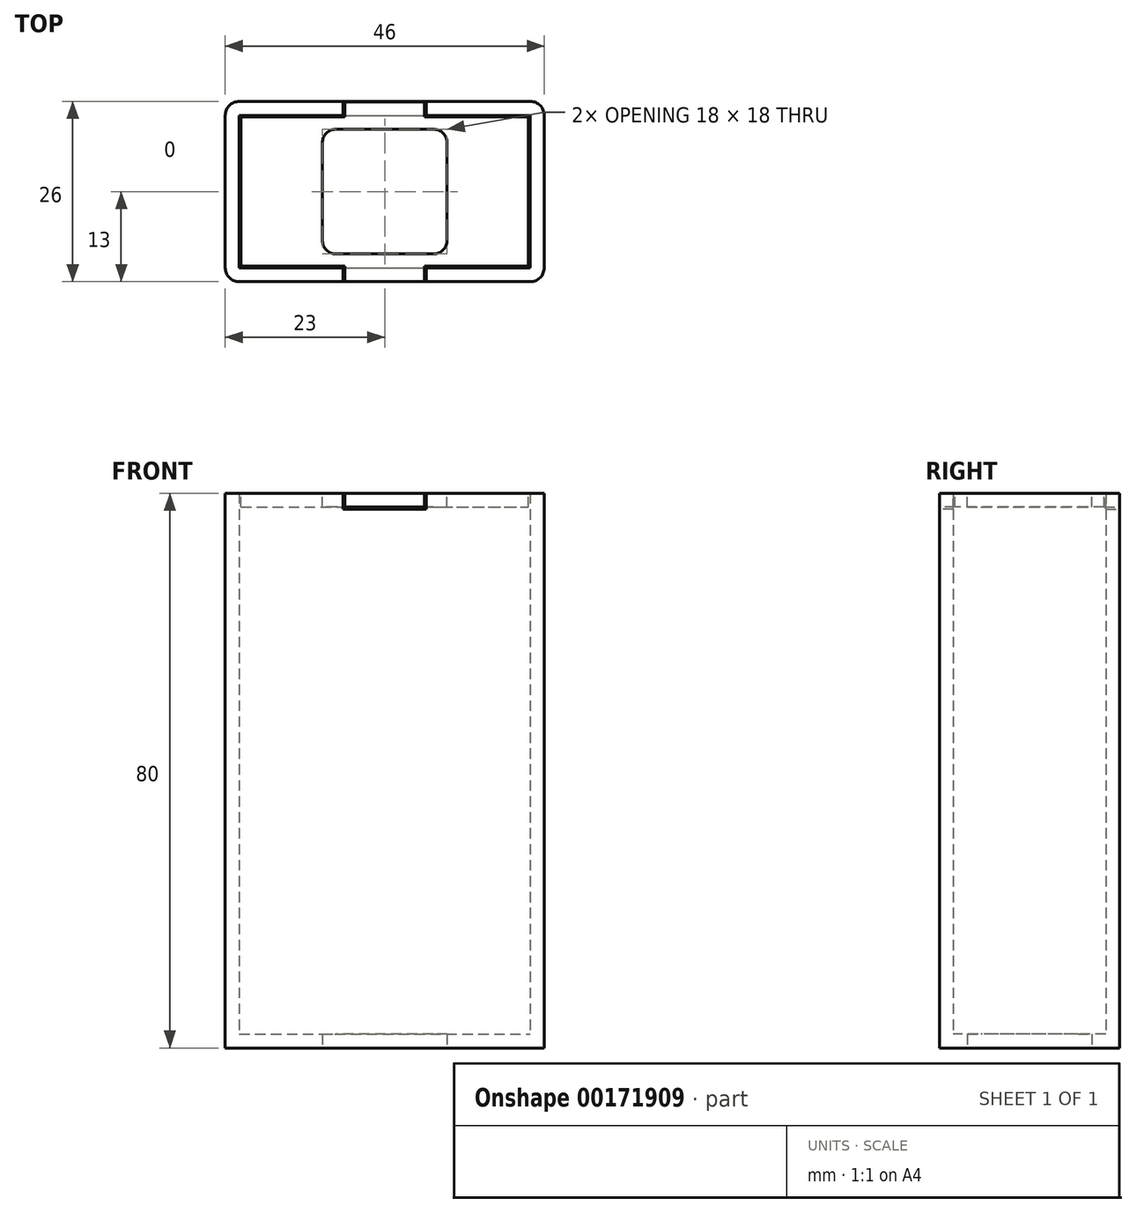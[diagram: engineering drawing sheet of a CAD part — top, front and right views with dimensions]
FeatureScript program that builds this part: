
annotation { "Feature Type Name" : "Feature", "Feature Type Description" : "" }
export const myFeature = defineFeature(function(context is Context, id is Id, definition is map)
    precondition{}
    {
        {
            var Q0;
            Q0=qCreatedBy(makeId("Top.planeOp"),FACE);
            var sketch = newSketch(context, id + "F0", { "sketchPlane" : qUnion([Q0])});
            skLineSegment(sketch, "E0.bottom", {"start": v(-23, 13) * mm, "end": v(23, 13) * mm});
            skLineSegment(sketch, "E0.top", {"start": v(-23, -13) * mm, "end": v(23, -13) * mm});
            skLineSegment(sketch, "E0.left", {"start": v(-23, 13) * mm, "end": v(-23, -13) * mm});
            skLineSegment(sketch, "E0.right", {"start": v(23, 13) * mm, "end": v(23, -13) * mm});
            skPoint(sketch, "E0.middle", {"position": v(0, 0) * mm});
            skSolve(sketch);
        }
        {
            var Q0;
            Q0 = qSketchRegion(id + "F0", true);
            extrude(context, id + "F1", {"entities" : qUnion([Q0]), "depth" : 80 * mm});
        }
        {
            var Q0;
            Q0=makeQuery(id+"F1.opExtrude","CAP_FACE",FACE,{"disambiguationData":[OSD([sQuery(id+"F0.wireOp",EDGE,"E0.bottom"),sQuery(id+"F0.wireOp",EDGE,"E0.top"),sQuery(id+"F0.wireOp",EDGE,"E0.left"),sQuery(id+"F0.wireOp",EDGE,"E0.right")])],"isStart":false});
            shell(context, id + "F2", {"entities" : qUnion([Q0]), "thickness" : 2 * mm});
        }
        {
            var Q0;
            Q0=makeQuery(id+"F1.opExtrude","CAP_FACE",FACE,{"disambiguationData":[OSD([sQuery(id+"F0.wireOp",EDGE,"E0.bottom"),sQuery(id+"F0.wireOp",EDGE,"E0.top"),sQuery(id+"F0.wireOp",EDGE,"E0.left"),sQuery(id+"F0.wireOp",EDGE,"E0.right")])],"isStart":false});
            var sketch = newSketch(context, id + "F3", { "sketchPlane" : qUnion([Q0])});
            skLineSegment(sketch, "E1.bottom", {"start": v(-6, 11) * mm, "end": v(6, 11) * mm});
            skLineSegment(sketch, "E1.top", {"start": v(-6, 13) * mm, "end": v(6, 13) * mm});
            skLineSegment(sketch, "E1.left", {"start": v(-6, 11) * mm, "end": v(-6, 13) * mm});
            skLineSegment(sketch, "E1.right", {"start": v(6, 11) * mm, "end": v(6, 13) * mm});
            skLineSegment(sketch, "E2.MirrorCS", {"start": v(-6, -13) * mm, "end": v(6, -13) * mm});
            skLineSegment(sketch, "E3.MirrorCS", {"start": v(-6, -11) * mm, "end": v(-6, -13) * mm});
            skLineSegment(sketch, "E4.MirrorCS", {"start": v(6, -11) * mm, "end": v(6, -13) * mm});
            skLineSegment(sketch, "E5.MirrorCS", {"start": v(-6, -11) * mm, "end": v(6, -11) * mm});
            skSolve(sketch);
        }
        {
            var Q0;
            Q0 = qSketchRegion(id + "F3", true);
            extrude(context, id + "F4", {"entities" : qUnion([Q0]), "operationType" : NewBodyOperationType.REMOVE, "oppositeDirection" : true, "depth" : 2.3 * mm});
        }
        {
            var Q0;
            Q0=qCreatedBy(makeId("Top.planeOp"),FACE);
            cPlane(context, id + "F5", {"entities" : qUnion([Q0]), "cplaneType" : CPlaneType.OFFSET, "offset" : 80 * mm, "width" : 150 * mm, "height" : 150 * mm});
        }
        {
            var Q0;
            Q0=qCreatedBy(id+"F5.planeOp",FACE);
            var sketch = newSketch(context, id + "F6", { "sketchPlane" : qUnion([Q0])});
            skLineSegment(sketch, "E6.bottom", {"start": v(-20.75, 10.75) * mm, "end": v(-5.75, 10.75) * mm});
            skLineSegment(sketch, "E6.top", {"start": v(-20.75, -10.75) * mm, "end": v(-5.75, -10.75) * mm});
            skLineSegment(sketch, "E6.left", {"start": v(-20.75, 10.75) * mm, "end": v(-20.75, -10.75) * mm});
            skLineSegment(sketch, "E6.right", {"start": v(20.75, 10.75) * mm, "end": v(20.75, -10.75) * mm});
            skPoint(sketch, "E6.middle", {"position": v(0, 0) * mm});
            skLineSegment(sketch, "E7.top", {"start": v(-5.75, 12.95) * mm, "end": v(5.75, 12.95) * mm});
            skLineSegment(sketch, "E7.left", {"start": v(-5.75, 10.75) * mm, "end": v(-5.75, 12.95) * mm});
            skLineSegment(sketch, "E7.right", {"start": v(5.75, 10.75) * mm, "end": v(5.75, 12.95) * mm});
            skLineSegment(sketch, "E8.MirrorCS", {"start": v(-5.75, -10.75) * mm, "end": v(-5.75, -12.95) * mm});
            skLineSegment(sketch, "E9.MirrorCS", {"start": v(-5.75, -12.95) * mm, "end": v(5.75, -12.95) * mm});
            skLineSegment(sketch, "E10.MirrorCS", {"start": v(5.75, -10.75) * mm, "end": v(5.75, -12.95) * mm});
            skPoint(sketch, "E11.MirrorCS.end.orphan", {"position": v(5.75, -10.75) * mm});
            skPoint(sketch, "E11.MirrorCS.start.orphan", {"position": v(-5.75, -10.75) * mm});
            skLineSegment(sketch, "E12.trimOffspring", {"start": v(5.75, -10.75) * mm, "end": v(20.75, -10.75) * mm});
            skLineSegment(sketch, "E13.trimOffspring", {"start": v(5.75, 10.75) * mm, "end": v(20.75, 10.75) * mm});
            skSolve(sketch);
        }
        {
            var Q0;
            Q0 = qSketchRegion(id + "F6", true);
            extrude(context, id + "F7", {"entities" : qUnion([Q0]), "oppositeDirection" : true, "depth" : 2 * mm});
        }
        {
            var Q0;
            Q0=makeQuery(id+"F1.opExtrude","SWEPT_EDGE",EDGE,{"disambiguationData":[OSD([sQuery(id+"F0.wireOp",EDGE,"E0.bottom"),sQuery(id+"F0.wireOp",EDGE,"E0.left")])]});
            var Q1;
            Q1=makeQuery(id+"F1.opExtrude","SWEPT_EDGE",EDGE,{"disambiguationData":[OSD([sQuery(id+"F0.wireOp",EDGE,"E0.bottom"),sQuery(id+"F0.wireOp",EDGE,"E0.right")])]});
            var Q2;
            Q2=makeQuery(id+"F1.opExtrude","SWEPT_EDGE",EDGE,{"disambiguationData":[OSD([sQuery(id+"F0.wireOp",EDGE,"E0.top"),sQuery(id+"F0.wireOp",EDGE,"E0.right")])]});
            var Q3;
            Q3=makeQuery(id+"F1.opExtrude","SWEPT_EDGE",EDGE,{"disambiguationData":[OSD([sQuery(id+"F0.wireOp",EDGE,"E0.top"),sQuery(id+"F0.wireOp",EDGE,"E0.left")])]});
            fillet(context, id + "F8", {"entities" : qUnion([Q0, Q1, Q2, Q3]), "radius" : 2 * mm, "tangentPropagation" : true, "allowEdgeOverflow" : false});
        }
        {
            var Q0;
            Q0=makeQuery(id+"F1.opExtrude","CAP_FACE",FACE,{"disambiguationData":[OSD([sQuery(id+"F0.wireOp",EDGE,"E0.bottom"),sQuery(id+"F0.wireOp",EDGE,"E0.top"),sQuery(id+"F0.wireOp",EDGE,"E0.left"),sQuery(id+"F0.wireOp",EDGE,"E0.right")])],"isStart":true});
            var sketch = newSketch(context, id + "F9", { "sketchPlane" : qUnion([Q0])});
            skCircle(sketch, "E14", {"center": v(0, 0) * mm, "radius": 5 * mm});
            skSolve(sketch);
        }
        {
            var Q0;
            Q0 = qSketchRegion(id + "F9", true);
            extrude(context, id + "F10", {"entities" : qUnion([Q0]), "operationType" : NewBodyOperationType.REMOVE, "oppositeDirection" : true, "depth" : 25 * mm});
        }
        {
            var Q0;
            Q0=makeQuery(id+"F7.opExtrude","CAP_FACE",FACE,{"disambiguationData":[OSD([sQuery(id+"F6.wireOp",EDGE,"E6.bottom"),sQuery(id+"F6.wireOp",EDGE,"E6.top"),sQuery(id+"F6.wireOp",EDGE,"E6.left"),sQuery(id+"F6.wireOp",EDGE,"E6.right"),sQuery(id+"F6.wireOp",EDGE,"E7.top"),sQuery(id+"F6.wireOp",EDGE,"E7.left"),sQuery(id+"F6.wireOp",EDGE,"E7.right"),sQuery(id+"F6.wireOp",EDGE,"E8.MirrorCS"),sQuery(id+"F6.wireOp",EDGE,"E9.MirrorCS"),sQuery(id+"F6.wireOp",EDGE,"E10.MirrorCS"),sQuery(id+"F6.wireOp",EDGE,"E12.trimOffspring"),sQuery(id+"F6.wireOp",EDGE,"E13.trimOffspring")])],"isStart":true});
            var sketch = newSketch(context, id + "F11", { "sketchPlane" : qUnion([Q0])});
            skLineSegment(sketch, "E15.bottom", {"start": v(9, -9) * mm, "end": v(-9, -9) * mm});
            skLineSegment(sketch, "E15.top", {"start": v(9, 9) * mm, "end": v(-9, 9) * mm});
            skLineSegment(sketch, "E15.left", {"start": v(9, -9) * mm, "end": v(9, 9) * mm});
            skLineSegment(sketch, "E15.right", {"start": v(-9, -9) * mm, "end": v(-9, 9) * mm});
            skPoint(sketch, "E15.middle", {"position": v(0, 0) * mm});
            skSolve(sketch);
        }
        {
            var Q0;
            Q0 = qSketchRegion(id + "F11", true);
            extrude(context, id + "F12", {"entities" : qUnion([Q0]), "operationType" : NewBodyOperationType.REMOVE, "oppositeDirection" : true, "depth" : 25 * mm});
        }
        {
            var Q0;
            Q0=makeQuery(id+"F12.boolean.opBoolean","COPY",EDGE,{"derivedFrom":makeQuery(id+"F12.opExtrude","SWEPT_EDGE",EDGE,{"disambiguationData":[OSD([sQuery(id+"F11.wireOp",EDGE,"E15.top"),sQuery(id+"F11.wireOp",EDGE,"E15.right")])]})});
            var Q1;
            Q1=makeQuery(id+"F12.boolean.opBoolean","COPY",EDGE,{"derivedFrom":makeQuery(id+"F12.opExtrude","SWEPT_EDGE",EDGE,{"disambiguationData":[OSD([sQuery(id+"F11.wireOp",EDGE,"E15.top"),sQuery(id+"F11.wireOp",EDGE,"E15.left")])]})});
            var Q2;
            Q2=makeQuery(id+"F12.boolean.opBoolean","COPY",EDGE,{"derivedFrom":makeQuery(id+"F12.opExtrude","SWEPT_EDGE",EDGE,{"disambiguationData":[OSD([sQuery(id+"F11.wireOp",EDGE,"E15.bottom"),sQuery(id+"F11.wireOp",EDGE,"E15.right")])]})});
            var Q3;
            Q3=makeQuery(id+"F12.boolean.opBoolean","COPY",EDGE,{"derivedFrom":makeQuery(id+"F12.opExtrude","SWEPT_EDGE",EDGE,{"disambiguationData":[OSD([sQuery(id+"F11.wireOp",EDGE,"E15.bottom"),sQuery(id+"F11.wireOp",EDGE,"E15.left")])]})});
            fillet(context, id + "F13", {"entities" : qUnion([Q0, Q1, Q2, Q3]), "radius" : 2 * mm, "tangentPropagation" : true, "allowEdgeOverflow" : false});
        }
        {
            var Q0;
            Q0=makeQuery(id+"F1.opExtrude","CAP_FACE",FACE,{"disambiguationData":[OSD([sQuery(id+"F0.wireOp",EDGE,"E0.bottom"),sQuery(id+"F0.wireOp",EDGE,"E0.top"),sQuery(id+"F0.wireOp",EDGE,"E0.left"),sQuery(id+"F0.wireOp",EDGE,"E0.right")])],"isStart":true});
            var sketch = newSketch(context, id + "F14", { "sketchPlane" : qUnion([Q0])});
            skLineSegment(sketch, "E16.bottom", {"start": v(-9, 9) * mm, "end": v(9, 9) * mm});
            skLineSegment(sketch, "E16.top", {"start": v(-9, -9) * mm, "end": v(9, -9) * mm});
            skLineSegment(sketch, "E16.left", {"start": v(-9, 9) * mm, "end": v(-9, -9) * mm});
            skLineSegment(sketch, "E16.right", {"start": v(9, 9) * mm, "end": v(9, -9) * mm});
            skPoint(sketch, "E16.middle", {"position": v(0, 0) * mm});
            skSolve(sketch);
        }
        {
            var Q0;
            Q0 = qSketchRegion(id + "F14", true);
            extrude(context, id + "F15", {"entities" : qUnion([Q0]), "operationType" : NewBodyOperationType.REMOVE, "oppositeDirection" : true, "depth" : 25 * mm});
        }
        {
            var Q0;
            Q0=makeQuery(id+"F15.boolean.opBoolean","COPY",EDGE,{"derivedFrom":makeQuery(id+"F15.opExtrude","SWEPT_EDGE",EDGE,{"disambiguationData":[OSD([sQuery(id+"F14.wireOp",EDGE,"E16.top"),sQuery(id+"F14.wireOp",EDGE,"E16.right")])]})});
            var Q1;
            Q1=makeQuery(id+"F15.boolean.opBoolean","COPY",EDGE,{"derivedFrom":makeQuery(id+"F15.opExtrude","SWEPT_EDGE",EDGE,{"disambiguationData":[OSD([sQuery(id+"F14.wireOp",EDGE,"E16.bottom"),sQuery(id+"F14.wireOp",EDGE,"E16.right")])]})});
            var Q2;
            Q2=makeQuery(id+"F15.boolean.opBoolean","COPY",EDGE,{"derivedFrom":makeQuery(id+"F15.opExtrude","SWEPT_EDGE",EDGE,{"disambiguationData":[OSD([sQuery(id+"F14.wireOp",EDGE,"E16.bottom"),sQuery(id+"F14.wireOp",EDGE,"E16.left")])]})});
            var Q3;
            Q3=makeQuery(id+"F15.boolean.opBoolean","COPY",EDGE,{"derivedFrom":makeQuery(id+"F15.opExtrude","SWEPT_EDGE",EDGE,{"disambiguationData":[OSD([sQuery(id+"F14.wireOp",EDGE,"E16.top"),sQuery(id+"F14.wireOp",EDGE,"E16.left")])]})});
            fillet(context, id + "F16", {"entities" : qUnion([Q0, Q1, Q2, Q3]), "radius" : 2 * mm, "tangentPropagation" : true, "allowEdgeOverflow" : false});
        }
    });
